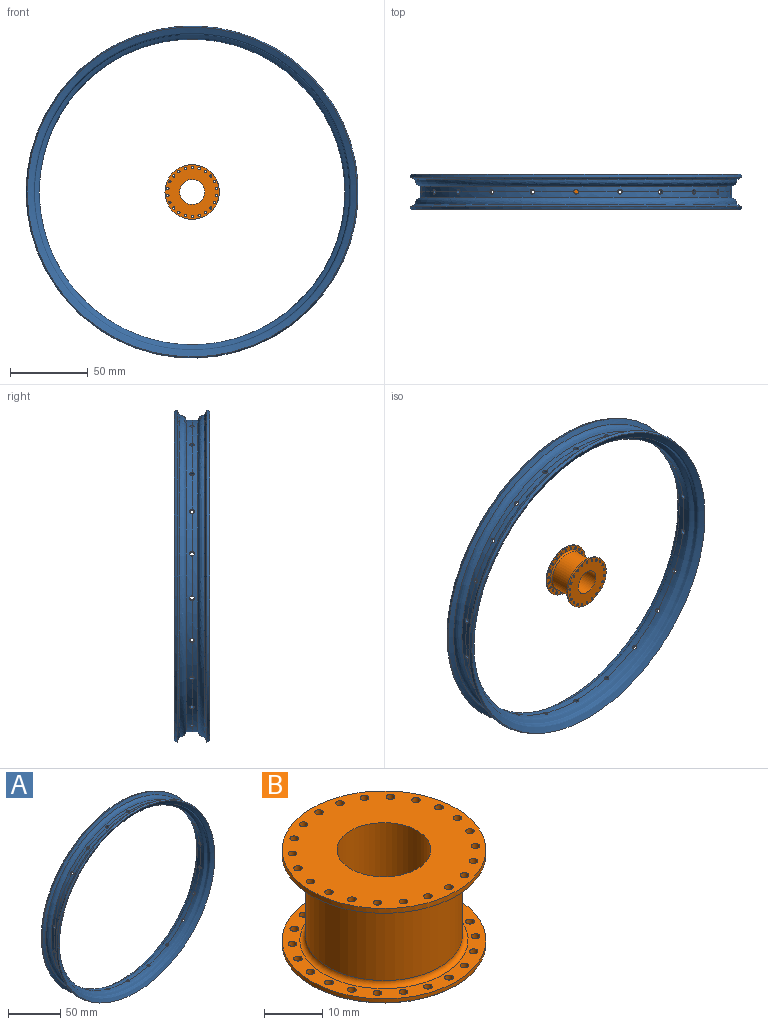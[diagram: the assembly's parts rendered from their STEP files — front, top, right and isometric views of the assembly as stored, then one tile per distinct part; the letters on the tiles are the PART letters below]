
ASSEMBLY  parts=2 mates=1
PART A: 32 faces, bbox 213.6x22.6x213.6 mm
  f0: cone r=106.08mm half-angle=21.7deg, axis (0,1,0), area 1337.7mm2, adj f3,f4
  f1: revolved ~199x199mm, area 4424.5mm2, adj f2,f6,f10,f11,f12,f13,f14,f15
  f2: revolved ~207.04x207.04mm, area 3673.2mm2, adj f1,f3
  f3: revolved ~213.65x213.65mm, area 2410mm2, adj f0,f2
  f4: revolved ~212.17x212.17mm, area 9710.2mm2, adj f0,f9,f10,f11,f12,f13,f14,f15
  f5: cone r=106.08mm half-angle=21.7deg, axis (0,-1,0), area 1337.7mm2, adj f8,f9
  f6: revolved ~200.16x200.16mm, area 2172.7mm2, adj f1,f7,f10,f11,f12,f13,f14,f15
  f7: revolved ~207.04x207.04mm, area 3673.2mm2, adj f6,f8
  f8: revolved ~213.65x213.65mm, area 4820mm2, adj f5,f7
  f9: revolved ~212.17x212.17mm, area 19499.6mm2, adj f4,f5,f10,f11,f12,f13,f14,f15
  f10: cylinder r=1.5mm len=3mm, axis (0,0,1), area 18.9mm2, adj f1,f4,f6,f9
  f11: cylinder r=1.5mm len=3.47mm, axis (-0.28,0,0.96), area 18.9mm2, adj f1,f4,f6,f9
  f12: cylinder r=1.5mm len=3.65mm, axis (-0.54,0,0.84), area 18.9mm2, adj f1,f4,f6,f9
  f13: cylinder r=1.5mm len=3.63mm, axis (-0.76,0,0.65), area 18.9mm2, adj f1,f4,f6,f9
  f14: cylinder r=1.5mm len=3.6mm, axis (-0.91,0,0.42), area 18.9mm2, adj f1,f4,f6,f9
  f15: cylinder r=1.5mm len=3.27mm, axis (-0.99,0,0.14), area 18.9mm2, adj f1,f4,f6,f9
  f16: cylinder r=1.5mm len=3.27mm, axis (-0.99,0,-0.14), area 18.9mm2, adj f1,f4,f6,f9
  f17: cylinder r=1.5mm len=3.6mm, axis (-0.91,0,-0.42), area 18.9mm2, adj f1,f4,f6,f9
  f18: cylinder r=1.5mm len=3.63mm, axis (-0.76,0,-0.65), area 18.9mm2, adj f1,f4,f6,f9
  f19: cylinder r=1.5mm len=3.65mm, axis (-0.54,0,-0.84), area 18.9mm2, adj f1,f4,f6,f9
  f20: cylinder r=1.5mm len=3.47mm, axis (-0.28,0,-0.96), area 18.9mm2, adj f1,f4,f6,f9
  f21: cylinder r=1.5mm len=3mm, axis (0,0,-1), area 18.9mm2, adj f1,f4,f6,f9
  f22: cylinder r=1.5mm len=3.47mm, axis (0.28,0,-0.96), area 18.9mm2, adj f1,f4,f6,f9
  f23: cylinder r=1.5mm len=3.65mm, axis (0.54,0,-0.84), area 18.9mm2, adj f1,f4,f6,f9
  f24: cylinder r=1.5mm len=3.63mm, axis (0.76,0,-0.65), area 18.9mm2, adj f1,f4,f6,f9
  f25: cylinder r=1.5mm len=3.6mm, axis (0.91,0,-0.42), area 18.9mm2, adj f1,f4,f6,f9
  f26: cylinder r=1.5mm len=3.27mm, axis (0.99,0,-0.14), area 18.9mm2, adj f1,f4,f6,f9
  f27: cylinder r=1.5mm len=3.27mm, axis (0.99,0,0.14), area 18.9mm2, adj f1,f4,f6,f9
  f28: cylinder r=1.5mm len=3.6mm, axis (0.91,0,0.42), area 18.9mm2, adj f1,f4,f6,f9
  f29: cylinder r=1.5mm len=3.63mm, axis (0.76,0,0.65), area 18.9mm2, adj f1,f4,f6,f9
  f30: cylinder r=1.5mm len=3.65mm, axis (0.54,0,0.84), area 18.9mm2, adj f1,f4,f6,f9
  f31: cylinder r=1.5mm len=3.47mm, axis (0.28,0,0.96), area 18.9mm2, adj f1,f4,f6,f9
PART B: 56 faces, bbox 35x35x20 mm
  f0: cylinder r=17.5mm len=35mm, axis (0,0,-1), area 110mm2, adj f1,f2
  f1: plane 35x35mm, normal (0,0,1), area 720.8mm2, adj f0,f9,f13,f15,f17,f19,f21,f23
  f2: plane 35x35mm, normal (0,0,-1), area 268.3mm2, adj f0,f4,f13,f15,f17,f19,f21,f23
  f3: plane 35x35mm, normal (0,0,1), area 268.3mm2, adj f6,f8,f12,f14,f16,f18,f20,f22
  f4: torus R=14.45mm, axis (0,0,1), area 136.4mm2, adj f2,f5
  f5: cylinder r=13.45mm len=26.9mm, axis (0,0,1), area 1352.3mm2, adj f4,f6
  f6: torus R=14.45mm, axis (0,0,1), area 136.4mm2, adj f3,f5
  f7: plane 34.6x34.6mm, normal (0,0,-1), area 688.7mm2, adj f10,f11,f12,f14,f16,f18,f20,f22
  f8: cylinder r=17.5mm len=35mm, axis (0,0,-1), area 88mm2, adj f3,f11
  f9: cylinder r=8.05mm len=19.8mm, axis (0,0,-1), area 1001.7mm2, adj f1,f10
  f10: cone r=8.05mm half-angle=45deg, axis (0,0,-1), area 14.5mm2, adj f7,f9
  f11: cone r=17.5mm half-angle=45deg, axis (0,0,1), area 30.9mm2, adj f7,f8
  f12: cylinder r=0.74mm len=1.48mm, axis (0,0,-1), area 4.6mm2, adj f3,f7
  f13: cylinder r=0.74mm len=1.48mm, axis (0,0,-1), area 4.6mm2, adj f1,f2
  f14: cylinder r=0.74mm len=1.48mm, axis (0,0,-1), area 4.6mm2, adj f3,f7
  f15: cylinder r=0.74mm len=1.48mm, axis (0,0,-1), area 4.6mm2, adj f1,f2
  f16: cylinder r=0.74mm len=1.48mm, axis (0,0,-1), area 4.6mm2, adj f3,f7
  f17: cylinder r=0.74mm len=1.48mm, axis (0,0,-1), area 4.6mm2, adj f1,f2
  f18: cylinder r=0.74mm len=1.48mm, axis (0,0,-1), area 4.6mm2, adj f3,f7
  f19: cylinder r=0.74mm len=1.48mm, axis (0,0,-1), area 4.6mm2, adj f1,f2
  f20: cylinder r=0.74mm len=1.48mm, axis (0,0,-1), area 4.6mm2, adj f3,f7
  f21: cylinder r=0.74mm len=1.48mm, axis (0,0,-1), area 4.6mm2, adj f1,f2
  f22: cylinder r=0.74mm len=1.48mm, axis (0,0,-1), area 4.6mm2, adj f3,f7
  f23: cylinder r=0.74mm len=1.48mm, axis (0,0,-1), area 4.6mm2, adj f1,f2
  f24: cylinder r=0.74mm len=1.48mm, axis (0,0,-1), area 4.6mm2, adj f3,f7
  f25: cylinder r=0.74mm len=1.48mm, axis (0,0,-1), area 4.6mm2, adj f1,f2
  f26: cylinder r=0.74mm len=1.48mm, axis (0,0,-1), area 4.6mm2, adj f3,f7
  f27: cylinder r=0.74mm len=1.48mm, axis (0,0,-1), area 4.6mm2, adj f1,f2
  f28: cylinder r=0.74mm len=1.48mm, axis (0,0,-1), area 4.6mm2, adj f3,f7
  f29: cylinder r=0.74mm len=1.48mm, axis (0,0,-1), area 4.6mm2, adj f1,f2
  f30: cylinder r=0.74mm len=1.48mm, axis (0,0,-1), area 4.6mm2, adj f3,f7
  f31: cylinder r=0.74mm len=1.48mm, axis (0,0,-1), area 4.6mm2, adj f1,f2
  f32: cylinder r=0.74mm len=1.48mm, axis (0,0,-1), area 4.6mm2, adj f3,f7
  f33: cylinder r=0.74mm len=1.48mm, axis (0,0,-1), area 4.6mm2, adj f1,f2
  f34: cylinder r=0.74mm len=1.48mm, axis (0,0,-1), area 4.6mm2, adj f3,f7
  f35: cylinder r=0.74mm len=1.48mm, axis (0,0,-1), area 4.6mm2, adj f1,f2
  f36: cylinder r=0.74mm len=1.48mm, axis (0,0,-1), area 4.6mm2, adj f3,f7
  f37: cylinder r=0.74mm len=1.48mm, axis (0,0,-1), area 4.6mm2, adj f1,f2
  f38: cylinder r=0.74mm len=1.48mm, axis (0,0,-1), area 4.6mm2, adj f3,f7
  f39: cylinder r=0.74mm len=1.48mm, axis (0,0,-1), area 4.6mm2, adj f1,f2
  f40: cylinder r=0.74mm len=1.48mm, axis (0,0,-1), area 4.6mm2, adj f3,f7
  f41: cylinder r=0.74mm len=1.48mm, axis (0,0,-1), area 4.6mm2, adj f1,f2
  f42: cylinder r=0.74mm len=1.48mm, axis (0,0,-1), area 4.6mm2, adj f3,f7
  f43: cylinder r=0.74mm len=1.48mm, axis (0,0,-1), area 4.6mm2, adj f1,f2
  f44: cylinder r=0.74mm len=1.48mm, axis (0,0,-1), area 4.6mm2, adj f3,f7
  f45: cylinder r=0.74mm len=1.48mm, axis (0,0,-1), area 4.6mm2, adj f1,f2
  f46: cylinder r=0.74mm len=1.48mm, axis (0,0,-1), area 4.6mm2, adj f3,f7
  f47: cylinder r=0.74mm len=1.48mm, axis (0,0,-1), area 4.6mm2, adj f1,f2
  f48: cylinder r=0.74mm len=1.48mm, axis (0,0,-1), area 4.6mm2, adj f3,f7
  f49: cylinder r=0.74mm len=1.48mm, axis (0,0,-1), area 4.6mm2, adj f1,f2
  f50: cylinder r=0.74mm len=1.48mm, axis (0,0,-1), area 4.6mm2, adj f3,f7
  f51: cylinder r=0.74mm len=1.48mm, axis (0,0,-1), area 4.6mm2, adj f1,f2
  f52: cylinder r=0.74mm len=1.48mm, axis (0,0,-1), area 4.6mm2, adj f3,f7
  f53: cylinder r=0.74mm len=1.48mm, axis (0,0,-1), area 4.6mm2, adj f1,f2
  f54: cylinder r=0.74mm len=1.48mm, axis (0,0,-1), area 4.6mm2, adj f3,f7
  f55: cylinder r=0.74mm len=1.48mm, axis (0,0,-1), area 4.6mm2, adj f1,f2
PLACE A t=(-7.6,-5.72,-1.99)mm
PLACE B rot(axis=(1,0,0),90deg) t=(-7.6,-5.72,-1.99)mm
MATE fastened B.f0 <-> A.f0  axis (0,-1,0) through (-7.6,-5.72,-1.99)mm
